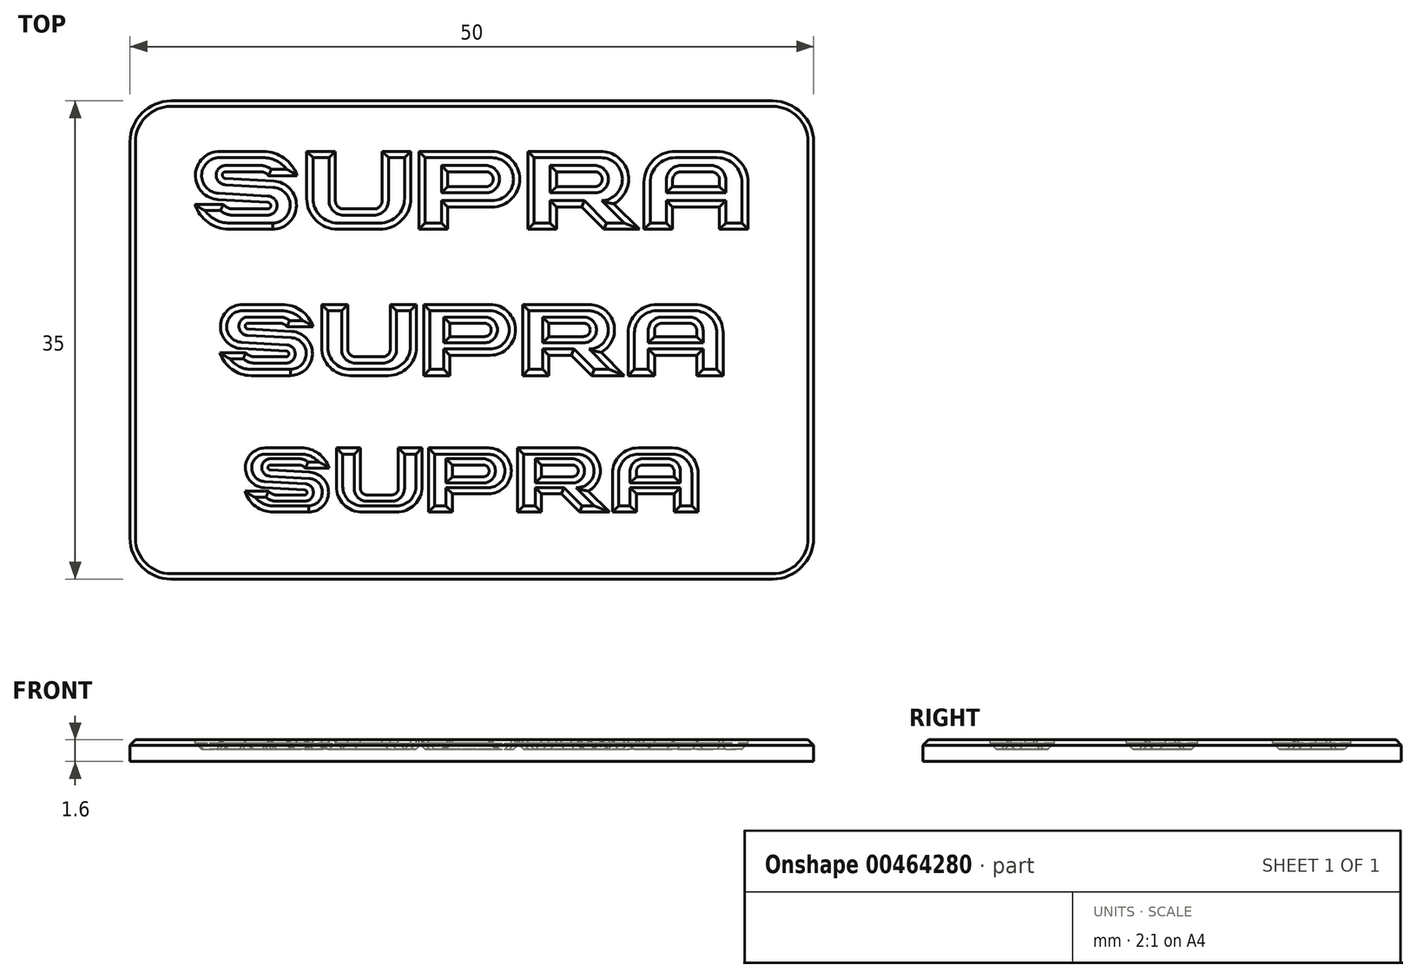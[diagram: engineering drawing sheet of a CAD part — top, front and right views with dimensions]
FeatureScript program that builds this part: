
annotation { "Feature Type Name" : "Feature", "Feature Type Description" : "" }
export const myFeature = defineFeature(function(context is Context, id is Id, definition is map)
    precondition{}
    {
        {
            var Q0;
            Q0=qCreatedBy(makeId("Top.planeOp"),FACE);
            var sketch = newSketch(context, id + "F0", { "sketchPlane" : qUnion([Q0])});
            skLineSegment(sketch, "E0.0", {"start": v(-11.75, 3.57) * mm, "end": v(-13.47, 3.57) * mm});
            skLineSegment(sketch, "E0.1", {"start": v(-14.02, 3.83) * mm, "end": v(-16.36, 3.83) * mm});
            skLineSegment(sketch, "E0.2", {"start": v(-15.88, 1.17) * mm, "end": v(-13.59, 1.17) * mm});
            skLineSegment(sketch, "E0.4", {"start": v(-16.57, 1.48) * mm, "end": v(-18.29, 1.48) * mm});
            skLineSegment(sketch, "E1", {"start": v(-16.86, 1.98) * mm, "end": v(-13.57, 1.8) * mm});
            skLineSegment(sketch, "E2", {"start": v(-16.38, 3.2) * mm, "end": v(-13.18, 3.03) * mm});
            skLineSegment(sketch, "E3.13", {"start": v(-6.12, 0) * mm, "end": v(-8.91, 0) * mm});
            skLineSegment(sketch, "E3.14", {"start": v(-8.52, 1.17) * mm, "end": v(-6.5, 1.17) * mm});
            skLineSegment(sketch, "E3.15", {"start": v(-9.17, 5) * mm, "end": v(-9.17, 1.81) * mm});
            skLineSegment(sketch, "E3.16", {"start": v(-10.89, 1.98) * mm, "end": v(-10.89, 5) * mm});
            skLineSegment(sketch, "E3.17", {"start": v(-10.89, 5) * mm, "end": v(-9.17, 5) * mm});
            skLineSegment(sketch, "E3.18", {"start": v(-5.87, 5) * mm, "end": v(-4.14, 5) * mm});
            skLineSegment(sketch, "E3.19", {"start": v(-4.14, 5) * mm, "end": v(-4.14, 1.98) * mm});
            skLineSegment(sketch, "E3.20", {"start": v(-5.87, 1.81) * mm, "end": v(-5.87, 5) * mm});
            skLineSegment(sketch, "E4.0", {"start": v(-3.42, 5) * mm, "end": v(1.34, 5) * mm});
            skLineSegment(sketch, "E4.1", {"start": v(0.94, 3.83) * mm, "end": v(-1.7, 3.83) * mm});
            skLineSegment(sketch, "E4.2", {"start": v(-1.7, 3.83) * mm, "end": v(-1.7, 2.66) * mm});
            skLineSegment(sketch, "E4.3", {"start": v(-1.7, 2.66) * mm, "end": v(0.94, 2.66) * mm});
            skLineSegment(sketch, "E4.4", {"start": v(1.34, 1.48) * mm, "end": v(-1.7, 1.48) * mm});
            skLineSegment(sketch, "E4.5", {"start": v(-1.7, 1.48) * mm, "end": v(-1.7, 0) * mm});
            skLineSegment(sketch, "E4.6", {"start": v(-3.42, 0) * mm, "end": v(-3.42, 5) * mm});
            skLineSegment(sketch, "E4.7", {"start": v(-1.7, 0) * mm, "end": v(-3.42, 0) * mm});
            skLineSegment(sketch, "E5.0", {"start": v(7.34, 1.48) * mm, "end": v(5.55, 1.48) * mm});
            skLineSegment(sketch, "E5.1", {"start": v(5.55, 1.48) * mm, "end": v(5.55, 0) * mm});
            skLineSegment(sketch, "E5.2", {"start": v(5.55, 0) * mm, "end": v(3.82, 0) * mm});
            skLineSegment(sketch, "E5.3", {"start": v(5.55, 2.66) * mm, "end": v(8.18, 2.66) * mm});
            skLineSegment(sketch, "E5.4", {"start": v(5.55, 3.83) * mm, "end": v(5.55, 2.66) * mm});
            skLineSegment(sketch, "E5.5", {"start": v(8.18, 3.83) * mm, "end": v(5.55, 3.83) * mm});
            skLineSegment(sketch, "E5.6", {"start": v(3.82, 5) * mm, "end": v(8.58, 5) * mm});
            skLineSegment(sketch, "E5.7", {"start": v(3.82, 0) * mm, "end": v(3.82, 5) * mm});
            skLineSegment(sketch, "E5.8", {"start": v(8.82, 0) * mm, "end": v(7.34, 1.48) * mm});
            skLineSegment(sketch, "E5.9", {"start": v(9.3, 1.63) * mm, "end": v(10.93, 0) * mm});
            skLineSegment(sketch, "E5.10", {"start": v(10.93, 0) * mm, "end": v(8.82, 0) * mm});
            skLineSegment(sketch, "E6.0", {"start": v(13.52, 5) * mm, "end": v(16.31, 5) * mm});
            skLineSegment(sketch, "E6.1", {"start": v(15.92, 3.83) * mm, "end": v(13.9, 3.83) * mm});
            skLineSegment(sketch, "E6.2", {"start": v(13.27, 3.19) * mm, "end": v(13.27, 2.66) * mm});
            skLineSegment(sketch, "E6.3", {"start": v(13.27, 2.66) * mm, "end": v(16.57, 2.66) * mm});
            skLineSegment(sketch, "E6.4", {"start": v(16.57, 2.66) * mm, "end": v(16.57, 3.19) * mm});
            skLineSegment(sketch, "E6.5", {"start": v(16.57, 1.48) * mm, "end": v(13.27, 1.48) * mm});
            skLineSegment(sketch, "E6.6", {"start": v(11.54, 0) * mm, "end": v(11.54, 3.02) * mm});
            skLineSegment(sketch, "E6.7", {"start": v(13.27, 0) * mm, "end": v(11.54, 0) * mm});
            skLineSegment(sketch, "E6.8", {"start": v(13.27, 1.48) * mm, "end": v(13.27, 0) * mm});
            skLineSegment(sketch, "E6.9", {"start": v(16.57, 0) * mm, "end": v(16.57, 1.48) * mm});
            skLineSegment(sketch, "E6.10", {"start": v(18.29, 0) * mm, "end": v(16.57, 0) * mm});
            skLineSegment(sketch, "E6.11", {"start": v(18.29, 3.02) * mm, "end": v(18.29, 0) * mm});
            skLineSegment(sketch, "E7", {"start": v(-7.52, 1.17) * mm, "end": v(-7.52, 0) * mm, "construction": true});
            skLineSegment(sketch, "E8", {"start": v(14.92, 3.83) * mm, "end": v(14.92, 5) * mm, "construction": true});
            skLineSegment(sketch, "E9", {"start": v(3.82, 0) * mm, "end": v(8.82, 0) * mm, "construction": true});
            skLineSegment(sketch, "E10", {"start": v(-1.7, 3.83) * mm, "end": v(-1.7, 5) * mm, "construction": true});
            skLineSegment(sketch, "E11", {"start": v(-1.7, 1.48) * mm, "end": v(-1.7, 2.66) * mm, "construction": true});
            skLineSegment(sketch, "E12", {"start": v(5.55, 1.48) * mm, "end": v(5.55, 2.66) * mm, "construction": true});
            skLineSegment(sketch, "E13", {"start": v(5.55, 3.83) * mm, "end": v(5.55, 5) * mm, "construction": true});
            skArc(sketch, "E14", {"start": v(-16.38, 3.2) * mm, "mid": v(-16.67, 3.52) * mm, "end": v(-16.36, 3.83) * mm});
            skArc(sketch, "E15", {"start": v(-14.02, 3.83) * mm, "mid": v(-13.72, 3.76) * mm, "end": v(-13.47, 3.57) * mm});
            skArc(sketch, "E16", {"start": v(-15.88, 1.17) * mm, "mid": v(-16.26, 1.25) * mm, "end": v(-16.57, 1.48) * mm});
            skArc(sketch, "E17", {"start": v(-13.57, 1.8) * mm, "mid": v(-13.27, 1.48) * mm, "end": v(-13.59, 1.17) * mm});
            skArc(sketch, "E18", {"start": v(-13.86, 5) * mm, "mid": v(-12.59, 4.61) * mm, "end": v(-11.75, 3.57) * mm});
            skArc(sketch, "E19", {"start": v(-16.13, 0) * mm, "mid": v(-17.44, 0.4) * mm, "end": v(-18.29, 1.48) * mm});
            skArc(sketch, "E20", {"start": v(-8.52, 1.17) * mm, "mid": v(-8.98, 1.36) * mm, "end": v(-9.17, 1.81) * mm});
            skArc(sketch, "E21", {"start": v(-6.5, 1.17) * mm, "mid": v(-6.05, 1.36) * mm, "end": v(-5.87, 1.81) * mm});
            skArc(sketch, "E22", {"start": v(-8.91, 0) * mm, "mid": v(-10.3, 0.58) * mm, "end": v(-10.89, 1.98) * mm});
            skArc(sketch, "E23", {"start": v(-6.12, 0) * mm, "mid": v(-4.72, 0.58) * mm, "end": v(-4.14, 1.98) * mm});
            skArc(sketch, "E24", {"start": v(1.34, 5) * mm, "mid": v(3.1, 3.24) * mm, "end": v(1.34, 1.48) * mm});
            skArc(sketch, "E25", {"start": v(0.94, 3.83) * mm, "mid": v(1.52, 3.24) * mm, "end": v(0.94, 2.66) * mm});
            skArc(sketch, "E26", {"start": v(8.18, 3.83) * mm, "mid": v(8.76, 3.24) * mm, "end": v(8.18, 2.66) * mm});
            skArc(sketch, "E27", {"start": v(13.9, 3.83) * mm, "mid": v(13.45, 3.64) * mm, "end": v(13.27, 3.19) * mm});
            skArc(sketch, "E28", {"start": v(15.92, 3.83) * mm, "mid": v(16.38, 3.64) * mm, "end": v(16.57, 3.19) * mm});
            skArc(sketch, "E29", {"start": v(13.52, 5) * mm, "mid": v(12.12, 4.42) * mm, "end": v(11.54, 3.02) * mm});
            skArc(sketch, "E30", {"start": v(16.31, 5) * mm, "mid": v(17.7, 4.42) * mm, "end": v(18.29, 3.02) * mm});
            skLineSegment(sketch, "E31", {"start": v(-9.17, 1.81) * mm, "end": v(-5.87, 1.81) * mm, "construction": true});
            skArc(sketch, "E32", {"start": v(8.58, 5) * mm, "mid": v(10.3, 3.6) * mm, "end": v(9.3, 1.63) * mm});
            skArc(sketch, "E33", {"start": v(-16.86, 1.98) * mm, "mid": v(-18.29, 3.53) * mm, "end": v(-16.78, 5) * mm});
            skLineSegment(sketch, "E34", {"start": v(-13.86, 5) * mm, "end": v(-16.78, 5) * mm});
            skArc(sketch, "E35", {"start": v(-13.18, 3.03) * mm, "mid": v(-11.75, 1.48) * mm, "end": v(-13.25, 0) * mm});
            skLineSegment(sketch, "E36", {"start": v(-16.13, 0) * mm, "end": v(-13.25, 0) * mm});
            skLineSegment(sketch, "E37.bottom", {"start": v(-18.29, 5) * mm, "end": v(18.29, 5) * mm, "construction": true});
            skLineSegment(sketch, "E37.top", {"start": v(-18.29, 0) * mm, "end": v(18.29, 0) * mm, "construction": true});
            skLineSegment(sketch, "E37.left", {"start": v(-18.29, 5) * mm, "end": v(-18.29, 0) * mm, "construction": true});
            skLineSegment(sketch, "E37.right", {"start": v(18.29, 5) * mm, "end": v(18.29, 0) * mm, "construction": true});
            skLineSegment(sketch, "E38", {"start": v(1.52, 3.24) * mm, "end": v(3.1, 3.24) * mm, "construction": true});
            skLineSegment(sketch, "E39", {"start": v(8.76, 3.24) * mm, "end": v(10.34, 3.24) * mm, "construction": true});
            skLineSegment(sketch, "E40", {"start": v(3.1, 3.24) * mm, "end": v(3.82, 3.24) * mm, "construction": true});
            skLineSegment(sketch, "E41", {"start": v(-4.14, 3.24) * mm, "end": v(-3.42, 3.24) * mm, "construction": true});
            skPoint(sketch, "E42", {"position": v(-11.75, 1.48) * mm});
            skSolve(sketch);
        }
        {
            var Q0;
            Q0=qCreatedBy(makeId("Top.planeOp"),FACE);
            var sketch = newSketch(context, id + "F1", { "sketchPlane" : qUnion([Q0])});
            skLineSegment(sketch, "E43.0", {"start": v(-12.93, 14.64) * mm, "end": v(-14.82, 14.64) * mm});
            skLineSegment(sketch, "E43.1", {"start": v(-15.43, 14.92) * mm, "end": v(-18, 14.92) * mm});
            skLineSegment(sketch, "E43.2", {"start": v(-17.47, 12) * mm, "end": v(-14.95, 12) * mm});
            skLineSegment(sketch, "E43.4", {"start": v(-18.22, 12.34) * mm, "end": v(-20.12, 12.34) * mm});
            skLineSegment(sketch, "E44", {"start": v(-18.54, 12.88) * mm, "end": v(-14.93, 12.68) * mm});
            skLineSegment(sketch, "E45", {"start": v(-18.02, 14.23) * mm, "end": v(-14.5, 14.04) * mm});
            skLineSegment(sketch, "E46.13", {"start": v(-6.73, 10.7) * mm, "end": v(-9.8, 10.7) * mm});
            skLineSegment(sketch, "E46.14", {"start": v(-9.37, 12) * mm, "end": v(-7.16, 12) * mm});
            skLineSegment(sketch, "E46.15", {"start": v(-10.08, 16.2) * mm, "end": v(-10.08, 12.7) * mm});
            skLineSegment(sketch, "E46.16", {"start": v(-11.98, 12.88) * mm, "end": v(-11.98, 16.2) * mm});
            skLineSegment(sketch, "E46.17", {"start": v(-11.98, 16.2) * mm, "end": v(-10.08, 16.2) * mm});
            skLineSegment(sketch, "E46.18", {"start": v(-6.45, 16.2) * mm, "end": v(-4.56, 16.2) * mm});
            skLineSegment(sketch, "E46.19", {"start": v(-4.56, 16.2) * mm, "end": v(-4.56, 12.88) * mm});
            skLineSegment(sketch, "E46.20", {"start": v(-6.45, 12.7) * mm, "end": v(-6.45, 16.2) * mm});
            skLineSegment(sketch, "E47.0", {"start": v(-3.76, 16.2) * mm, "end": v(1.48, 16.2) * mm});
            skLineSegment(sketch, "E47.1", {"start": v(1.03, 14.92) * mm, "end": v(-1.87, 14.92) * mm});
            skLineSegment(sketch, "E47.2", {"start": v(-1.87, 14.92) * mm, "end": v(-1.87, 13.63) * mm});
            skLineSegment(sketch, "E47.3", {"start": v(-1.87, 13.63) * mm, "end": v(1.03, 13.63) * mm});
            skLineSegment(sketch, "E47.4", {"start": v(1.48, 12.34) * mm, "end": v(-1.87, 12.34) * mm});
            skLineSegment(sketch, "E47.5", {"start": v(-1.87, 12.34) * mm, "end": v(-1.87, 10.7) * mm});
            skLineSegment(sketch, "E47.6", {"start": v(-3.76, 10.7) * mm, "end": v(-3.76, 16.2) * mm});
            skLineSegment(sketch, "E47.7", {"start": v(-1.87, 10.7) * mm, "end": v(-3.76, 10.7) * mm});
            skLineSegment(sketch, "E48.0", {"start": v(8.07, 12.34) * mm, "end": v(6.1, 12.34) * mm});
            skLineSegment(sketch, "E48.1", {"start": v(6.1, 12.34) * mm, "end": v(6.1, 10.7) * mm});
            skLineSegment(sketch, "E48.2", {"start": v(6.1, 10.7) * mm, "end": v(4.2, 10.7) * mm});
            skLineSegment(sketch, "E48.3", {"start": v(6.1, 13.63) * mm, "end": v(9, 13.63) * mm});
            skLineSegment(sketch, "E48.4", {"start": v(6.1, 14.92) * mm, "end": v(6.1, 13.63) * mm});
            skLineSegment(sketch, "E48.5", {"start": v(9, 14.92) * mm, "end": v(6.1, 14.92) * mm});
            skLineSegment(sketch, "E48.6", {"start": v(4.2, 16.2) * mm, "end": v(9.44, 16.2) * mm});
            skLineSegment(sketch, "E48.7", {"start": v(4.2, 10.7) * mm, "end": v(4.2, 16.2) * mm});
            skLineSegment(sketch, "E48.8", {"start": v(9.7, 10.7) * mm, "end": v(8.07, 12.34) * mm});
            skLineSegment(sketch, "E48.9", {"start": v(10.22, 12.5) * mm, "end": v(12.02, 10.7) * mm});
            skLineSegment(sketch, "E48.10", {"start": v(12.02, 10.7) * mm, "end": v(9.7, 10.7) * mm});
            skLineSegment(sketch, "E49.0", {"start": v(14.87, 16.2) * mm, "end": v(17.94, 16.2) * mm});
            skLineSegment(sketch, "E49.1", {"start": v(17.51, 14.92) * mm, "end": v(15.3, 14.92) * mm});
            skLineSegment(sketch, "E49.2", {"start": v(14.6, 14.2) * mm, "end": v(14.6, 13.63) * mm});
            skLineSegment(sketch, "E49.3", {"start": v(14.6, 13.63) * mm, "end": v(18.22, 13.63) * mm});
            skLineSegment(sketch, "E49.4", {"start": v(18.22, 13.63) * mm, "end": v(18.22, 14.2) * mm});
            skLineSegment(sketch, "E49.5", {"start": v(18.22, 12.34) * mm, "end": v(14.6, 12.34) * mm});
            skLineSegment(sketch, "E49.6", {"start": v(12.7, 10.7) * mm, "end": v(12.7, 14.03) * mm});
            skLineSegment(sketch, "E49.7", {"start": v(14.6, 10.7) * mm, "end": v(12.7, 10.7) * mm});
            skLineSegment(sketch, "E49.8", {"start": v(14.6, 12.34) * mm, "end": v(14.6, 10.7) * mm});
            skLineSegment(sketch, "E49.9", {"start": v(18.22, 10.7) * mm, "end": v(18.22, 12.34) * mm});
            skLineSegment(sketch, "E49.10", {"start": v(20.12, 10.7) * mm, "end": v(18.22, 10.7) * mm});
            skLineSegment(sketch, "E49.11", {"start": v(20.12, 14.03) * mm, "end": v(20.12, 10.7) * mm});
            skLineSegment(sketch, "E50", {"start": v(-8.27, 12) * mm, "end": v(-8.27, 10.7) * mm, "construction": true});
            skLineSegment(sketch, "E51", {"start": v(16.4, 14.92) * mm, "end": v(16.4, 16.2) * mm, "construction": true});
            skLineSegment(sketch, "E52", {"start": v(4.2, 10.7) * mm, "end": v(9.7, 10.7) * mm, "construction": true});
            skLineSegment(sketch, "E53", {"start": v(-1.87, 14.92) * mm, "end": v(-1.87, 16.2) * mm, "construction": true});
            skLineSegment(sketch, "E54", {"start": v(-1.87, 12.34) * mm, "end": v(-1.87, 13.63) * mm, "construction": true});
            skLineSegment(sketch, "E55", {"start": v(6.1, 12.34) * mm, "end": v(6.1, 13.63) * mm, "construction": true});
            skLineSegment(sketch, "E56", {"start": v(6.1, 14.92) * mm, "end": v(6.1, 16.2) * mm, "construction": true});
            skArc(sketch, "E57", {"start": v(-18.02, 14.23) * mm, "mid": v(-18.34, 14.58) * mm, "end": v(-18, 14.92) * mm});
            skArc(sketch, "E58", {"start": v(-15.43, 14.92) * mm, "mid": v(-15.1, 14.84) * mm, "end": v(-14.82, 14.64) * mm});
            skArc(sketch, "E59", {"start": v(-17.47, 12) * mm, "mid": v(-17.88, 12.09) * mm, "end": v(-18.22, 12.34) * mm});
            skArc(sketch, "E60", {"start": v(-14.93, 12.68) * mm, "mid": v(-14.6, 12.33) * mm, "end": v(-14.95, 12) * mm});
            skArc(sketch, "E61", {"start": v(-15.25, 16.2) * mm, "mid": v(-13.85, 15.78) * mm, "end": v(-12.93, 14.64) * mm});
            skArc(sketch, "E62", {"start": v(-17.74, 10.7) * mm, "mid": v(-19.19, 11.15) * mm, "end": v(-20.12, 12.34) * mm});
            skArc(sketch, "E63", {"start": v(-9.37, 12) * mm, "mid": v(-9.87, 12.2) * mm, "end": v(-10.08, 12.7) * mm});
            skArc(sketch, "E64", {"start": v(-7.16, 12) * mm, "mid": v(-6.66, 12.2) * mm, "end": v(-6.45, 12.7) * mm});
            skArc(sketch, "E65", {"start": v(-9.8, 10.7) * mm, "mid": v(-11.34, 11.34) * mm, "end": v(-11.98, 12.88) * mm});
            skArc(sketch, "E66", {"start": v(-6.73, 10.7) * mm, "mid": v(-5.2, 11.34) * mm, "end": v(-4.56, 12.88) * mm});
            skArc(sketch, "E67", {"start": v(1.48, 16.2) * mm, "mid": v(3.4, 14.27) * mm, "end": v(1.48, 12.34) * mm});
            skArc(sketch, "E68", {"start": v(1.03, 14.92) * mm, "mid": v(1.67, 14.27) * mm, "end": v(1.03, 13.63) * mm});
            skArc(sketch, "E69", {"start": v(9, 14.92) * mm, "mid": v(9.64, 14.27) * mm, "end": v(9, 13.63) * mm});
            skArc(sketch, "E70", {"start": v(15.3, 14.92) * mm, "mid": v(14.8, 14.7) * mm, "end": v(14.6, 14.2) * mm});
            skArc(sketch, "E71", {"start": v(17.51, 14.92) * mm, "mid": v(18.01, 14.7) * mm, "end": v(18.22, 14.2) * mm});
            skArc(sketch, "E72", {"start": v(14.87, 16.2) * mm, "mid": v(13.33, 15.57) * mm, "end": v(12.7, 14.03) * mm});
            skArc(sketch, "E73", {"start": v(17.94, 16.2) * mm, "mid": v(19.48, 15.57) * mm, "end": v(20.12, 14.03) * mm});
            skLineSegment(sketch, "E74", {"start": v(-10.08, 12.7) * mm, "end": v(-6.45, 12.7) * mm, "construction": true});
            skArc(sketch, "E75", {"start": v(9.44, 16.2) * mm, "mid": v(11.33, 14.67) * mm, "end": v(10.22, 12.5) * mm});
            skArc(sketch, "E76", {"start": v(-18.54, 12.88) * mm, "mid": v(-20.12, 14.59) * mm, "end": v(-18.45, 16.2) * mm});
            skLineSegment(sketch, "E77", {"start": v(-15.25, 16.2) * mm, "end": v(-18.45, 16.2) * mm});
            skArc(sketch, "E78", {"start": v(-14.5, 14.04) * mm, "mid": v(-12.93, 12.34) * mm, "end": v(-14.57, 10.7) * mm});
            skLineSegment(sketch, "E79", {"start": v(-17.74, 10.7) * mm, "end": v(-14.57, 10.7) * mm});
            skLineSegment(sketch, "E80.bottom", {"start": v(-20.12, 16.2) * mm, "end": v(20.12, 16.2) * mm, "construction": true});
            skLineSegment(sketch, "E80.top", {"start": v(-20.12, 10.7) * mm, "end": v(20.12, 10.7) * mm, "construction": true});
            skLineSegment(sketch, "E80.left", {"start": v(-20.12, 16.2) * mm, "end": v(-20.12, 10.7) * mm, "construction": true});
            skLineSegment(sketch, "E80.right", {"start": v(20.12, 16.2) * mm, "end": v(20.12, 10.7) * mm, "construction": true});
            skLineSegment(sketch, "E81", {"start": v(1.67, 14.27) * mm, "end": v(3.4, 14.27) * mm, "construction": true});
            skLineSegment(sketch, "E82", {"start": v(9.64, 14.27) * mm, "end": v(11.38, 14.27) * mm, "construction": true});
            skLineSegment(sketch, "E83", {"start": v(3.4, 14.27) * mm, "end": v(4.2, 14.27) * mm, "construction": true});
            skLineSegment(sketch, "E84", {"start": v(-4.56, 14.27) * mm, "end": v(-3.76, 14.27) * mm, "construction": true});
            skPoint(sketch, "E85", {"position": v(-12.93, 12.34) * mm});
            skSolve(sketch);
        }
        {
            var Q0;
            Q0=qCreatedBy(makeId("Top.planeOp"),FACE);
            var sketch = newSketch(context, id + "F2", { "sketchPlane" : qUnion([Q0])});
            skLineSegment(sketch, "E86.0", {"start": v(-10.58, -6.78) * mm, "end": v(-12.13, -6.78) * mm});
            skLineSegment(sketch, "E86.1", {"start": v(-12.62, -6.55) * mm, "end": v(-14.73, -6.55) * mm});
            skLineSegment(sketch, "E86.2", {"start": v(-14.3, -8.94) * mm, "end": v(-12.23, -8.94) * mm});
            skLineSegment(sketch, "E86.4", {"start": v(-14.9, -8.66) * mm, "end": v(-16.46, -8.66) * mm});
            skLineSegment(sketch, "E87", {"start": v(-15.17, -8.21) * mm, "end": v(-12.21, -8.38) * mm});
            skLineSegment(sketch, "E88", {"start": v(-14.74, -7.1) * mm, "end": v(-11.86, -7.27) * mm});
            skLineSegment(sketch, "E89.13", {"start": v(-5.5, -10) * mm, "end": v(-8.02, -10) * mm});
            skLineSegment(sketch, "E89.14", {"start": v(-7.67, -8.94) * mm, "end": v(-5.86, -8.94) * mm});
            skLineSegment(sketch, "E89.15", {"start": v(-8.25, -5.5) * mm, "end": v(-8.25, -8.36) * mm});
            skLineSegment(sketch, "E89.16", {"start": v(-9.8, -8.21) * mm, "end": v(-9.8, -5.5) * mm});
            skLineSegment(sketch, "E89.17", {"start": v(-9.8, -5.5) * mm, "end": v(-8.25, -5.5) * mm});
            skLineSegment(sketch, "E89.18", {"start": v(-5.28, -5.5) * mm, "end": v(-3.73, -5.5) * mm});
            skLineSegment(sketch, "E89.19", {"start": v(-3.73, -5.5) * mm, "end": v(-3.73, -8.21) * mm});
            skLineSegment(sketch, "E89.20", {"start": v(-5.28, -8.36) * mm, "end": v(-5.28, -5.5) * mm});
            skLineSegment(sketch, "E90.0", {"start": v(-3.08, -5.5) * mm, "end": v(1.2, -5.5) * mm});
            skLineSegment(sketch, "E90.1", {"start": v(0.84, -6.55) * mm, "end": v(-1.53, -6.55) * mm});
            skLineSegment(sketch, "E90.2", {"start": v(-1.53, -6.55) * mm, "end": v(-1.53, -7.6) * mm});
            skLineSegment(sketch, "E90.3", {"start": v(-1.53, -7.6) * mm, "end": v(0.84, -7.6) * mm});
            skLineSegment(sketch, "E90.4", {"start": v(1.2, -8.66) * mm, "end": v(-1.53, -8.66) * mm});
            skLineSegment(sketch, "E90.5", {"start": v(-1.53, -8.66) * mm, "end": v(-1.53, -10) * mm});
            skLineSegment(sketch, "E90.6", {"start": v(-3.08, -10) * mm, "end": v(-3.08, -5.5) * mm});
            skLineSegment(sketch, "E90.7", {"start": v(-1.53, -10) * mm, "end": v(-3.08, -10) * mm});
            skLineSegment(sketch, "E91.0", {"start": v(6.6, -8.66) * mm, "end": v(5, -8.66) * mm});
            skLineSegment(sketch, "E91.1", {"start": v(5, -8.66) * mm, "end": v(5, -10) * mm});
            skLineSegment(sketch, "E91.2", {"start": v(5, -10) * mm, "end": v(3.44, -10) * mm});
            skLineSegment(sketch, "E91.3", {"start": v(5, -7.6) * mm, "end": v(7.36, -7.6) * mm});
            skLineSegment(sketch, "E91.4", {"start": v(5, -6.55) * mm, "end": v(5, -7.6) * mm});
            skLineSegment(sketch, "E91.5", {"start": v(7.36, -6.55) * mm, "end": v(5, -6.55) * mm});
            skLineSegment(sketch, "E91.6", {"start": v(3.44, -5.5) * mm, "end": v(7.73, -5.5) * mm});
            skLineSegment(sketch, "E91.7", {"start": v(3.44, -10) * mm, "end": v(3.44, -5.5) * mm});
            skLineSegment(sketch, "E91.8", {"start": v(7.94, -10) * mm, "end": v(6.6, -8.66) * mm});
            skLineSegment(sketch, "E91.9", {"start": v(8.36, -8.52) * mm, "end": v(9.83, -10) * mm});
            skLineSegment(sketch, "E91.10", {"start": v(9.83, -10) * mm, "end": v(7.94, -10) * mm});
            skLineSegment(sketch, "E92.0", {"start": v(12.17, -5.5) * mm, "end": v(14.68, -5.5) * mm});
            skLineSegment(sketch, "E92.1", {"start": v(14.33, -6.55) * mm, "end": v(12.52, -6.55) * mm});
            skLineSegment(sketch, "E92.2", {"start": v(11.94, -7.13) * mm, "end": v(11.94, -7.6) * mm});
            skLineSegment(sketch, "E92.3", {"start": v(11.94, -7.6) * mm, "end": v(14.9, -7.6) * mm});
            skLineSegment(sketch, "E92.4", {"start": v(14.9, -7.6) * mm, "end": v(14.9, -7.13) * mm});
            skLineSegment(sketch, "E92.5", {"start": v(14.9, -8.66) * mm, "end": v(11.94, -8.66) * mm});
            skLineSegment(sketch, "E92.6", {"start": v(10.39, -10) * mm, "end": v(10.39, -7.27) * mm});
            skLineSegment(sketch, "E92.7", {"start": v(11.94, -10) * mm, "end": v(10.39, -10) * mm});
            skLineSegment(sketch, "E92.8", {"start": v(11.94, -8.66) * mm, "end": v(11.94, -10) * mm});
            skLineSegment(sketch, "E92.9", {"start": v(14.9, -10) * mm, "end": v(14.9, -8.66) * mm});
            skLineSegment(sketch, "E92.10", {"start": v(16.46, -10) * mm, "end": v(14.9, -10) * mm});
            skLineSegment(sketch, "E92.11", {"start": v(16.46, -7.27) * mm, "end": v(16.46, -10) * mm});
            skLineSegment(sketch, "E93", {"start": v(-6.76, -8.94) * mm, "end": v(-6.76, -10) * mm, "construction": true});
            skLineSegment(sketch, "E94", {"start": v(13.42, -6.55) * mm, "end": v(13.42, -5.5) * mm, "construction": true});
            skLineSegment(sketch, "E95", {"start": v(3.44, -10) * mm, "end": v(7.94, -10) * mm, "construction": true});
            skLineSegment(sketch, "E96", {"start": v(-1.53, -6.55) * mm, "end": v(-1.53, -5.5) * mm, "construction": true});
            skLineSegment(sketch, "E97", {"start": v(-1.53, -8.66) * mm, "end": v(-1.53, -7.6) * mm, "construction": true});
            skLineSegment(sketch, "E98", {"start": v(5, -8.66) * mm, "end": v(5, -7.6) * mm, "construction": true});
            skLineSegment(sketch, "E99", {"start": v(5, -6.55) * mm, "end": v(5, -5.5) * mm, "construction": true});
            skArc(sketch, "E100", {"start": v(-14.74, -7.1) * mm, "mid": v(-15, -6.82) * mm, "end": v(-14.73, -6.55) * mm});
            skArc(sketch, "E101", {"start": v(-12.62, -6.55) * mm, "mid": v(-12.35, -6.6) * mm, "end": v(-12.13, -6.78) * mm});
            skArc(sketch, "E102", {"start": v(-14.3, -8.94) * mm, "mid": v(-14.63, -8.86) * mm, "end": v(-14.9, -8.66) * mm});
            skArc(sketch, "E103", {"start": v(-12.21, -8.38) * mm, "mid": v(-11.95, -8.67) * mm, "end": v(-12.23, -8.94) * mm});
            skArc(sketch, "E104", {"start": v(-12.48, -5.5) * mm, "mid": v(-11.33, -5.84) * mm, "end": v(-10.58, -6.78) * mm});
            skArc(sketch, "E105", {"start": v(-14.52, -10) * mm, "mid": v(-15.7, -9.63) * mm, "end": v(-16.46, -8.66) * mm});
            skArc(sketch, "E106", {"start": v(-7.67, -8.94) * mm, "mid": v(-8.08, -8.77) * mm, "end": v(-8.25, -8.36) * mm});
            skArc(sketch, "E107", {"start": v(-5.86, -8.94) * mm, "mid": v(-5.45, -8.77) * mm, "end": v(-5.28, -8.36) * mm});
            skArc(sketch, "E108", {"start": v(-8.02, -10) * mm, "mid": v(-9.28, -9.47) * mm, "end": v(-9.8, -8.21) * mm});
            skArc(sketch, "E109", {"start": v(-5.5, -10) * mm, "mid": v(-4.25, -9.47) * mm, "end": v(-3.73, -8.21) * mm});
            skArc(sketch, "E110", {"start": v(1.2, -5.5) * mm, "mid": v(2.79, -7.08) * mm, "end": v(1.2, -8.66) * mm});
            skArc(sketch, "E111", {"start": v(0.84, -6.55) * mm, "mid": v(1.37, -7.08) * mm, "end": v(0.84, -7.6) * mm});
            skArc(sketch, "E112", {"start": v(7.36, -6.55) * mm, "mid": v(7.89, -7.08) * mm, "end": v(7.36, -7.6) * mm});
            skArc(sketch, "E113", {"start": v(12.52, -6.55) * mm, "mid": v(12.1, -6.72) * mm, "end": v(11.94, -7.13) * mm});
            skArc(sketch, "E114", {"start": v(14.33, -6.55) * mm, "mid": v(14.74, -6.72) * mm, "end": v(14.9, -7.13) * mm});
            skArc(sketch, "E115", {"start": v(12.17, -5.5) * mm, "mid": v(10.9, -6.01) * mm, "end": v(10.39, -7.27) * mm});
            skArc(sketch, "E116", {"start": v(14.68, -5.5) * mm, "mid": v(15.94, -6.01) * mm, "end": v(16.46, -7.27) * mm});
            skLineSegment(sketch, "E117", {"start": v(-8.25, -8.36) * mm, "end": v(-5.28, -8.36) * mm, "construction": true});
            skArc(sketch, "E118", {"start": v(7.73, -5.5) * mm, "mid": v(9.27, -6.75) * mm, "end": v(8.36, -8.52) * mm});
            skArc(sketch, "E119", {"start": v(-15.17, -8.21) * mm, "mid": v(-16.46, -6.82) * mm, "end": v(-15.1, -5.5) * mm});
            skLineSegment(sketch, "E120", {"start": v(-12.48, -5.5) * mm, "end": v(-15.1, -5.5) * mm});
            skArc(sketch, "E121", {"start": v(-11.86, -7.27) * mm, "mid": v(-10.58, -8.66) * mm, "end": v(-11.92, -10) * mm});
            skLineSegment(sketch, "E122", {"start": v(-14.52, -10) * mm, "end": v(-11.92, -10) * mm});
            skLineSegment(sketch, "E123.bottom", {"start": v(-16.46, -5.5) * mm, "end": v(16.46, -5.5) * mm, "construction": true});
            skLineSegment(sketch, "E123.top", {"start": v(-16.46, -10) * mm, "end": v(16.46, -10) * mm, "construction": true});
            skLineSegment(sketch, "E123.left", {"start": v(-16.46, -5.5) * mm, "end": v(-16.46, -10) * mm, "construction": true});
            skLineSegment(sketch, "E123.right", {"start": v(16.46, -5.5) * mm, "end": v(16.46, -10) * mm, "construction": true});
            skLineSegment(sketch, "E124", {"start": v(1.37, -7.08) * mm, "end": v(2.79, -7.08) * mm, "construction": true});
            skLineSegment(sketch, "E125", {"start": v(7.89, -7.08) * mm, "end": v(9.3, -7.08) * mm, "construction": true});
            skLineSegment(sketch, "E126", {"start": v(2.79, -7.08) * mm, "end": v(3.44, -7.08) * mm, "construction": true});
            skLineSegment(sketch, "E127", {"start": v(-3.73, -7.08) * mm, "end": v(-3.08, -7.08) * mm, "construction": true});
            skPoint(sketch, "E128", {"position": v(-10.58, -8.66) * mm});
            skSolve(sketch);
        }
        {
            var Q0;
            Q0 = qSketchRegion(id + "F0", true);
            var Q1;
            Q1 = qSketchRegion(id + "F1", true);
            var Q2;
            Q2 = qSketchRegion(id + "F2", true);
            extrude(context, id + "F3", {"entities" : qUnion([Q0, Q1, Q2]), "oppositeDirection" : true, "depth" : 0.6 * mm, "offsetDistance" : 25 * mm});
        }
        {
            var Q0;
            Q0=qCreatedBy(makeId("Top.planeOp"),FACE);
            var sketch = newSketch(context, id + "F4", { "sketchPlane" : qUnion([Q0])});
            skLineSegment(sketch, "E129.bottom", {"start": v(22, -15) * mm, "end": v(-22, -15) * mm});
            skLineSegment(sketch, "E129.top", {"start": v(22, 20) * mm, "end": v(-22, 20) * mm});
            skLineSegment(sketch, "E129.left", {"start": v(25, -12) * mm, "end": v(25, 17) * mm});
            skLineSegment(sketch, "E129.right", {"start": v(-25, -12) * mm, "end": v(-25, 17) * mm});
            skPoint(sketch, "E129.middle", {"position": v(0, 2.5) * mm});
            skPoint(sketch, "E130.visualSharp", {"position": v(-25, 20) * mm});
            skArc(sketch, "E130.filletArc", {"start": v(-22, 20) * mm, "mid": v(-24.12, 19.12) * mm, "end": v(-25, 17) * mm});
            skPoint(sketch, "E131.visualSharp", {"position": v(-25, -15) * mm});
            skArc(sketch, "E131.filletArc", {"start": v(-25, -12) * mm, "mid": v(-24.12, -14.12) * mm, "end": v(-22, -15) * mm});
            skPoint(sketch, "E132.visualSharp", {"position": v(25, -15) * mm});
            skArc(sketch, "E132.filletArc", {"start": v(22, -15) * mm, "mid": v(24.12, -14.12) * mm, "end": v(25, -12) * mm});
            skPoint(sketch, "E133.visualSharp", {"position": v(25, 20) * mm});
            skArc(sketch, "E133.filletArc", {"start": v(25, 17) * mm, "mid": v(24.12, 19.12) * mm, "end": v(22, 20) * mm});
            skSolve(sketch);
        }
        {
            var Q0;
            Q0 = qSketchRegion(id + "F4", true);
            extrude(context, id + "F5", {"entities" : qUnion([Q0]), "oppositeDirection" : true, "depth" : 1.6 * mm, "offsetDistance" : 25 * mm});
        }
        {
            var Q0;
            Q0=makeQuery(id+"F3.opExtrude","CAP_FACE",FACE,{"disambiguationData":[OSD([sQuery(id+"F0.wireOp",EDGE,"E0.0"),sQuery(id+"F0.wireOp",EDGE,"E0.1"),sQuery(id+"F0.wireOp",EDGE,"E0.2"),sQuery(id+"F0.wireOp",EDGE,"E0.3"),sQuery(id+"F0.wireOp",EDGE,"E0.4"),sQuery(id+"F0.wireOp",EDGE,"0999620a-5725-4c23-bbf2-5b95b2830843"),sQuery(id+"F0.wireOp",EDGE,"386d07d4-47ab-48fc-b2f3-6c93ff8b900a"),sQuery(id+"F0.wireOp",EDGE,"7d214aef-e285-4256-be08-b174b5a9389a"),sQuery(id+"F0.wireOp",EDGE,"1d019c9d-348e-44f8-a51e-25f3e83873e8"),sQuery(id+"F0.wireOp",EDGE,"8814e4d5-f851-4526-9bd3-24134bf95cf7"),sQuery(id+"F0.wireOp",EDGE,"854dbfa7-0297-4156-a36c-3462ac4aca29"),sQuery(id+"F0.wireOp",EDGE,"68418355-34de-4963-a5e1-fe12fbad6afa"),sQuery(id+"F0.wireOp",EDGE,"0ad70b45-b280-4e47-a12a-156df6aa18f4"),sQuery(id+"F0.wireOp",EDGE,"909f7516-75d9-4176-a7ec-8d11efcea972.0"),sQuery(id+"F0.wireOp",EDGE,"E1"),sQuery(id+"F0.wireOp",EDGE,"E2")])],"isStart":false});
            var Q1;
            Q1=makeQuery(id+"F3.opExtrude","CAP_FACE",FACE,{"disambiguationData":[OSD([sQuery(id+"F0.wireOp",EDGE,"E3.13"),sQuery(id+"F0.wireOp",EDGE,"E3.14"),sQuery(id+"F0.wireOp",EDGE,"E3.15"),sQuery(id+"F0.wireOp",EDGE,"E3.16"),sQuery(id+"F0.wireOp",EDGE,"E3.17"),sQuery(id+"F0.wireOp",EDGE,"E3.18"),sQuery(id+"F0.wireOp",EDGE,"E3.19"),sQuery(id+"F0.wireOp",EDGE,"E3.20"),sQuery(id+"F0.wireOp",EDGE,"18193e6a-b45a-4486-8c24-13befce3e4da"),sQuery(id+"F0.wireOp",EDGE,"87248437-bed7-459e-b474-820dd873d0e6"),sQuery(id+"F0.wireOp",EDGE,"dfc161e1-bacf-4af8-9d18-555532bfa341"),sQuery(id+"F0.wireOp",EDGE,"dfd43905-2174-4bfa-a2d9-08ca3ab83ac5")])],"isStart":false});
            var Q2;
            Q2=makeQuery(id+"F3.opExtrude","CAP_FACE",FACE,{"disambiguationData":[OSD([sQuery(id+"F0.wireOp",EDGE,"E4.0"),sQuery(id+"F0.wireOp",EDGE,"E4.1"),sQuery(id+"F0.wireOp",EDGE,"E4.2"),sQuery(id+"F0.wireOp",EDGE,"E4.3"),sQuery(id+"F0.wireOp",EDGE,"E4.4"),sQuery(id+"F0.wireOp",EDGE,"E4.5"),sQuery(id+"F0.wireOp",EDGE,"E4.6"),sQuery(id+"F0.wireOp",EDGE,"E4.7"),sQuery(id+"F0.wireOp",EDGE,"109b3e3a-7d6f-4e72-87ea-cb87c5d67c68"),sQuery(id+"F0.wireOp",EDGE,"418c2995-c520-4838-b757-5a34ee8e35cc")])],"isStart":false});
            var Q3;
            Q3=makeQuery(id+"F3.opExtrude","CAP_FACE",FACE,{"disambiguationData":[OSD([sQuery(id+"F0.wireOp",EDGE,"E5.0"),sQuery(id+"F0.wireOp",EDGE,"E5.1"),sQuery(id+"F0.wireOp",EDGE,"E5.2"),sQuery(id+"F0.wireOp",EDGE,"E5.3"),sQuery(id+"F0.wireOp",EDGE,"E5.4"),sQuery(id+"F0.wireOp",EDGE,"E5.5"),sQuery(id+"F0.wireOp",EDGE,"E5.6"),sQuery(id+"F0.wireOp",EDGE,"E5.7"),sQuery(id+"F0.wireOp",EDGE,"E5.8"),sQuery(id+"F0.wireOp",EDGE,"E5.9"),sQuery(id+"F0.wireOp",EDGE,"E5.10"),sQuery(id+"F0.wireOp",EDGE,"826e8434-5312-4b00-bb0e-243ee4ab690c"),sQuery(id+"F0.wireOp",EDGE,"61057553-3613-4276-97cf-7665bd9cf830")])],"isStart":false});
            var Q4;
            Q4=makeQuery(id+"F3.opExtrude","CAP_FACE",FACE,{"disambiguationData":[OSD([sQuery(id+"F0.wireOp",EDGE,"E6.0"),sQuery(id+"F0.wireOp",EDGE,"E6.1"),sQuery(id+"F0.wireOp",EDGE,"E6.2"),sQuery(id+"F0.wireOp",EDGE,"E6.3"),sQuery(id+"F0.wireOp",EDGE,"E6.4"),sQuery(id+"F0.wireOp",EDGE,"E6.5"),sQuery(id+"F0.wireOp",EDGE,"E6.6"),sQuery(id+"F0.wireOp",EDGE,"E6.7"),sQuery(id+"F0.wireOp",EDGE,"E6.8"),sQuery(id+"F0.wireOp",EDGE,"E6.9"),sQuery(id+"F0.wireOp",EDGE,"E6.10"),sQuery(id+"F0.wireOp",EDGE,"E6.11"),sQuery(id+"F0.wireOp",EDGE,"99e759a4-61d7-4b6e-b7ee-9723b9a24aa8"),sQuery(id+"F0.wireOp",EDGE,"a95c86a1-a8cb-4604-8402-e9795dd98b0d"),sQuery(id+"F0.wireOp",EDGE,"d81874d2-dd95-4ed2-8042-69ce277cbfb6"),sQuery(id+"F0.wireOp",EDGE,"669a06dd-cf1c-428e-8a50-f27afc4aee4d")])],"isStart":false});
            var Q5;
            Q5=makeQuery(id+"F3.opExtrude","CAP_FACE",FACE,{"disambiguationData":[OSD([sQuery(id+"F2.wireOp",EDGE,"E92.0"),sQuery(id+"F2.wireOp",EDGE,"E92.1"),sQuery(id+"F2.wireOp",EDGE,"E92.2"),sQuery(id+"F2.wireOp",EDGE,"E92.3"),sQuery(id+"F2.wireOp",EDGE,"E92.4"),sQuery(id+"F2.wireOp",EDGE,"E92.5"),sQuery(id+"F2.wireOp",EDGE,"E92.6"),sQuery(id+"F2.wireOp",EDGE,"E92.7"),sQuery(id+"F2.wireOp",EDGE,"E92.8"),sQuery(id+"F2.wireOp",EDGE,"E92.9"),sQuery(id+"F2.wireOp",EDGE,"E92.10"),sQuery(id+"F2.wireOp",EDGE,"E92.11"),sQuery(id+"F2.wireOp",EDGE,"E113"),sQuery(id+"F2.wireOp",EDGE,"E114"),sQuery(id+"F2.wireOp",EDGE,"E115"),sQuery(id+"F2.wireOp",EDGE,"E116")])],"isStart":false});
            var Q6;
            Q6=makeQuery(id+"F3.opExtrude","CAP_FACE",FACE,{"disambiguationData":[OSD([sQuery(id+"F2.wireOp",EDGE,"E91.0"),sQuery(id+"F2.wireOp",EDGE,"E91.1"),sQuery(id+"F2.wireOp",EDGE,"E91.2"),sQuery(id+"F2.wireOp",EDGE,"E91.3"),sQuery(id+"F2.wireOp",EDGE,"E91.4"),sQuery(id+"F2.wireOp",EDGE,"E91.5"),sQuery(id+"F2.wireOp",EDGE,"E91.6"),sQuery(id+"F2.wireOp",EDGE,"E91.7"),sQuery(id+"F2.wireOp",EDGE,"E91.8"),sQuery(id+"F2.wireOp",EDGE,"E91.9"),sQuery(id+"F2.wireOp",EDGE,"E91.10"),sQuery(id+"F2.wireOp",EDGE,"E112"),sQuery(id+"F2.wireOp",EDGE,"E118")])],"isStart":false});
            var Q7;
            Q7=makeQuery(id+"F3.opExtrude","CAP_FACE",FACE,{"disambiguationData":[OSD([sQuery(id+"F2.wireOp",EDGE,"E90.0"),sQuery(id+"F2.wireOp",EDGE,"E90.1"),sQuery(id+"F2.wireOp",EDGE,"E90.2"),sQuery(id+"F2.wireOp",EDGE,"E90.3"),sQuery(id+"F2.wireOp",EDGE,"E90.4"),sQuery(id+"F2.wireOp",EDGE,"E90.5"),sQuery(id+"F2.wireOp",EDGE,"E90.6"),sQuery(id+"F2.wireOp",EDGE,"E90.7"),sQuery(id+"F2.wireOp",EDGE,"E110"),sQuery(id+"F2.wireOp",EDGE,"E111")])],"isStart":false});
            var Q8;
            Q8=makeQuery(id+"F3.opExtrude","CAP_FACE",FACE,{"disambiguationData":[OSD([sQuery(id+"F2.wireOp",EDGE,"E89.13"),sQuery(id+"F2.wireOp",EDGE,"E89.14"),sQuery(id+"F2.wireOp",EDGE,"E89.15"),sQuery(id+"F2.wireOp",EDGE,"E89.16"),sQuery(id+"F2.wireOp",EDGE,"E89.17"),sQuery(id+"F2.wireOp",EDGE,"E89.18"),sQuery(id+"F2.wireOp",EDGE,"E89.19"),sQuery(id+"F2.wireOp",EDGE,"E89.20"),sQuery(id+"F2.wireOp",EDGE,"E106"),sQuery(id+"F2.wireOp",EDGE,"E107"),sQuery(id+"F2.wireOp",EDGE,"E108"),sQuery(id+"F2.wireOp",EDGE,"E109")])],"isStart":false});
            var Q9;
            Q9=makeQuery(id+"F3.opExtrude","CAP_FACE",FACE,{"disambiguationData":[OSD([sQuery(id+"F2.wireOp",EDGE,"E86.0"),sQuery(id+"F2.wireOp",EDGE,"E86.1"),sQuery(id+"F2.wireOp",EDGE,"E86.2"),sQuery(id+"F2.wireOp",EDGE,"E86.4"),sQuery(id+"F2.wireOp",EDGE,"E87"),sQuery(id+"F2.wireOp",EDGE,"E88"),sQuery(id+"F2.wireOp",EDGE,"E100"),sQuery(id+"F2.wireOp",EDGE,"E101"),sQuery(id+"F2.wireOp",EDGE,"E102"),sQuery(id+"F2.wireOp",EDGE,"E103"),sQuery(id+"F2.wireOp",EDGE,"E104"),sQuery(id+"F2.wireOp",EDGE,"E105"),sQuery(id+"F2.wireOp",EDGE,"E119"),sQuery(id+"F2.wireOp",EDGE,"E120"),sQuery(id+"F2.wireOp",EDGE,"E121"),sQuery(id+"F2.wireOp",EDGE,"E122")])],"isStart":false});
            var Q10;
            Q10=makeQuery(id+"F3.opExtrude","CAP_FACE",FACE,{"disambiguationData":[OSD([sQuery(id+"F1.wireOp",EDGE,"E49.0"),sQuery(id+"F1.wireOp",EDGE,"E49.1"),sQuery(id+"F1.wireOp",EDGE,"E49.2"),sQuery(id+"F1.wireOp",EDGE,"E49.3"),sQuery(id+"F1.wireOp",EDGE,"E49.4"),sQuery(id+"F1.wireOp",EDGE,"E49.5"),sQuery(id+"F1.wireOp",EDGE,"E49.6"),sQuery(id+"F1.wireOp",EDGE,"E49.7"),sQuery(id+"F1.wireOp",EDGE,"E49.8"),sQuery(id+"F1.wireOp",EDGE,"E49.9"),sQuery(id+"F1.wireOp",EDGE,"E49.10"),sQuery(id+"F1.wireOp",EDGE,"E49.11"),sQuery(id+"F1.wireOp",EDGE,"E70"),sQuery(id+"F1.wireOp",EDGE,"E71"),sQuery(id+"F1.wireOp",EDGE,"E72"),sQuery(id+"F1.wireOp",EDGE,"E73")])],"isStart":false});
            var Q11;
            Q11=makeQuery(id+"F3.opExtrude","CAP_FACE",FACE,{"disambiguationData":[OSD([sQuery(id+"F1.wireOp",EDGE,"E48.0"),sQuery(id+"F1.wireOp",EDGE,"E48.1"),sQuery(id+"F1.wireOp",EDGE,"E48.2"),sQuery(id+"F1.wireOp",EDGE,"E48.3"),sQuery(id+"F1.wireOp",EDGE,"E48.4"),sQuery(id+"F1.wireOp",EDGE,"E48.5"),sQuery(id+"F1.wireOp",EDGE,"E48.6"),sQuery(id+"F1.wireOp",EDGE,"E48.7"),sQuery(id+"F1.wireOp",EDGE,"E48.8"),sQuery(id+"F1.wireOp",EDGE,"E48.9"),sQuery(id+"F1.wireOp",EDGE,"E48.10"),sQuery(id+"F1.wireOp",EDGE,"E69"),sQuery(id+"F1.wireOp",EDGE,"E75")])],"isStart":false});
            var Q12;
            Q12=makeQuery(id+"F3.opExtrude","CAP_FACE",FACE,{"disambiguationData":[OSD([sQuery(id+"F1.wireOp",EDGE,"E47.0"),sQuery(id+"F1.wireOp",EDGE,"E47.1"),sQuery(id+"F1.wireOp",EDGE,"E47.2"),sQuery(id+"F1.wireOp",EDGE,"E47.3"),sQuery(id+"F1.wireOp",EDGE,"E47.4"),sQuery(id+"F1.wireOp",EDGE,"E47.5"),sQuery(id+"F1.wireOp",EDGE,"E47.6"),sQuery(id+"F1.wireOp",EDGE,"E47.7"),sQuery(id+"F1.wireOp",EDGE,"E67"),sQuery(id+"F1.wireOp",EDGE,"E68")])],"isStart":false});
            var Q13;
            Q13=makeQuery(id+"F3.opExtrude","CAP_FACE",FACE,{"disambiguationData":[OSD([sQuery(id+"F1.wireOp",EDGE,"E46.13"),sQuery(id+"F1.wireOp",EDGE,"E46.14"),sQuery(id+"F1.wireOp",EDGE,"E46.15"),sQuery(id+"F1.wireOp",EDGE,"E46.16"),sQuery(id+"F1.wireOp",EDGE,"E46.17"),sQuery(id+"F1.wireOp",EDGE,"E46.18"),sQuery(id+"F1.wireOp",EDGE,"E46.19"),sQuery(id+"F1.wireOp",EDGE,"E46.20"),sQuery(id+"F1.wireOp",EDGE,"E63"),sQuery(id+"F1.wireOp",EDGE,"E64"),sQuery(id+"F1.wireOp",EDGE,"E65"),sQuery(id+"F1.wireOp",EDGE,"E66")])],"isStart":false});
            var Q14;
            Q14=makeQuery(id+"F3.opExtrude","CAP_FACE",FACE,{"disambiguationData":[OSD([sQuery(id+"F1.wireOp",EDGE,"E43.0"),sQuery(id+"F1.wireOp",EDGE,"E43.1"),sQuery(id+"F1.wireOp",EDGE,"E43.2"),sQuery(id+"F1.wireOp",EDGE,"E43.4"),sQuery(id+"F1.wireOp",EDGE,"E44"),sQuery(id+"F1.wireOp",EDGE,"E45"),sQuery(id+"F1.wireOp",EDGE,"E57"),sQuery(id+"F1.wireOp",EDGE,"E58"),sQuery(id+"F1.wireOp",EDGE,"E59"),sQuery(id+"F1.wireOp",EDGE,"E60"),sQuery(id+"F1.wireOp",EDGE,"E61"),sQuery(id+"F1.wireOp",EDGE,"E62"),sQuery(id+"F1.wireOp",EDGE,"E76"),sQuery(id+"F1.wireOp",EDGE,"E77"),sQuery(id+"F1.wireOp",EDGE,"E78"),sQuery(id+"F1.wireOp",EDGE,"E79")])],"isStart":false});
            var Q15;
            Q15=makeQuery(id+"F5.opExtrude","CAP_FACE",FACE,{"disambiguationData":[OSD([sQuery(id+"F4.wireOp",EDGE,"E129.bottom"),sQuery(id+"F4.wireOp",EDGE,"E129.top"),sQuery(id+"F4.wireOp",EDGE,"E129.left"),sQuery(id+"F4.wireOp",EDGE,"E129.right"),sQuery(id+"F4.wireOp",EDGE,"E130.filletArc"),sQuery(id+"F4.wireOp",EDGE,"E131.filletArc"),sQuery(id+"F4.wireOp",EDGE,"E132.filletArc"),sQuery(id+"F4.wireOp",EDGE,"E133.filletArc")])],"isStart":true});
            chamfer(context, id + "F6", {"entities" : qUnion([Q0, Q1, Q2, Q3, Q4, Q5, Q6, Q7, Q8, Q9, Q10, Q11, Q12, Q13, Q14, Q15]), "width" : 0.4 * mm, "tangentPropagation" : true});
        }
        {
            var Q0;
            Q0=makeQuery(id+"F3.opExtrude","SWEPT_BODY",BODY,{"disambiguationData":[OSD([sQuery(id+"F0.wireOp",EDGE,"E0.0"),sQuery(id+"F0.wireOp",EDGE,"E0.1"),sQuery(id+"F0.wireOp",EDGE,"E0.2"),sQuery(id+"F0.wireOp",EDGE,"E0.4"),sQuery(id+"F0.wireOp",EDGE,"E1"),sQuery(id+"F0.wireOp",EDGE,"E2"),sQuery(id+"F0.wireOp",EDGE,"E14"),sQuery(id+"F0.wireOp",EDGE,"E15"),sQuery(id+"F0.wireOp",EDGE,"E16"),sQuery(id+"F0.wireOp",EDGE,"E17"),sQuery(id+"F0.wireOp",EDGE,"E18"),sQuery(id+"F0.wireOp",EDGE,"E19"),sQuery(id+"F0.wireOp",EDGE,"E33"),sQuery(id+"F0.wireOp",EDGE,"E34"),sQuery(id+"F0.wireOp",EDGE,"E35"),sQuery(id+"F0.wireOp",EDGE,"E36")])]});
            var Q1;
            Q1=makeQuery(id+"F3.opExtrude","SWEPT_BODY",BODY,{"disambiguationData":[OSD([sQuery(id+"F0.wireOp",EDGE,"E3.13"),sQuery(id+"F0.wireOp",EDGE,"E3.14"),sQuery(id+"F0.wireOp",EDGE,"E3.15"),sQuery(id+"F0.wireOp",EDGE,"E3.16"),sQuery(id+"F0.wireOp",EDGE,"E3.17"),sQuery(id+"F0.wireOp",EDGE,"E3.18"),sQuery(id+"F0.wireOp",EDGE,"E3.19"),sQuery(id+"F0.wireOp",EDGE,"E3.20"),sQuery(id+"F0.wireOp",EDGE,"E20"),sQuery(id+"F0.wireOp",EDGE,"E21"),sQuery(id+"F0.wireOp",EDGE,"E22"),sQuery(id+"F0.wireOp",EDGE,"E23")])]});
            var Q2;
            Q2=makeQuery(id+"F3.opExtrude","SWEPT_BODY",BODY,{"disambiguationData":[OSD([sQuery(id+"F0.wireOp",EDGE,"E4.0"),sQuery(id+"F0.wireOp",EDGE,"E4.1"),sQuery(id+"F0.wireOp",EDGE,"E4.2"),sQuery(id+"F0.wireOp",EDGE,"E4.3"),sQuery(id+"F0.wireOp",EDGE,"E4.4"),sQuery(id+"F0.wireOp",EDGE,"E4.5"),sQuery(id+"F0.wireOp",EDGE,"E4.6"),sQuery(id+"F0.wireOp",EDGE,"E4.7"),sQuery(id+"F0.wireOp",EDGE,"E24"),sQuery(id+"F0.wireOp",EDGE,"E25")])]});
            var Q3;
            Q3=makeQuery(id+"F3.opExtrude","SWEPT_BODY",BODY,{"disambiguationData":[OSD([sQuery(id+"F0.wireOp",EDGE,"E5.0"),sQuery(id+"F0.wireOp",EDGE,"E5.1"),sQuery(id+"F0.wireOp",EDGE,"E5.2"),sQuery(id+"F0.wireOp",EDGE,"E5.3"),sQuery(id+"F0.wireOp",EDGE,"E5.4"),sQuery(id+"F0.wireOp",EDGE,"E5.5"),sQuery(id+"F0.wireOp",EDGE,"E5.6"),sQuery(id+"F0.wireOp",EDGE,"E5.7"),sQuery(id+"F0.wireOp",EDGE,"E5.8"),sQuery(id+"F0.wireOp",EDGE,"E5.9"),sQuery(id+"F0.wireOp",EDGE,"E5.10"),sQuery(id+"F0.wireOp",EDGE,"E26"),sQuery(id+"F0.wireOp",EDGE,"E32")])]});
            var Q4;
            Q4=makeQuery(id+"F3.opExtrude","SWEPT_BODY",BODY,{"disambiguationData":[OSD([sQuery(id+"F0.wireOp",EDGE,"E6.0"),sQuery(id+"F0.wireOp",EDGE,"E6.1"),sQuery(id+"F0.wireOp",EDGE,"E6.2"),sQuery(id+"F0.wireOp",EDGE,"E6.3"),sQuery(id+"F0.wireOp",EDGE,"E6.4"),sQuery(id+"F0.wireOp",EDGE,"E6.5"),sQuery(id+"F0.wireOp",EDGE,"E6.6"),sQuery(id+"F0.wireOp",EDGE,"E6.7"),sQuery(id+"F0.wireOp",EDGE,"E6.8"),sQuery(id+"F0.wireOp",EDGE,"E6.9"),sQuery(id+"F0.wireOp",EDGE,"E6.10"),sQuery(id+"F0.wireOp",EDGE,"E6.11"),sQuery(id+"F0.wireOp",EDGE,"E27"),sQuery(id+"F0.wireOp",EDGE,"E28"),sQuery(id+"F0.wireOp",EDGE,"E29"),sQuery(id+"F0.wireOp",EDGE,"E30")])]});
            var Q5;
            Q5=makeQuery(id+"F3.opExtrude","SWEPT_BODY",BODY,{"disambiguationData":[OSD([sQuery(id+"F1.wireOp",EDGE,"E43.0"),sQuery(id+"F1.wireOp",EDGE,"E43.1"),sQuery(id+"F1.wireOp",EDGE,"E43.2"),sQuery(id+"F1.wireOp",EDGE,"E43.4"),sQuery(id+"F1.wireOp",EDGE,"E44"),sQuery(id+"F1.wireOp",EDGE,"E45"),sQuery(id+"F1.wireOp",EDGE,"E57"),sQuery(id+"F1.wireOp",EDGE,"E58"),sQuery(id+"F1.wireOp",EDGE,"E59"),sQuery(id+"F1.wireOp",EDGE,"E60"),sQuery(id+"F1.wireOp",EDGE,"E61"),sQuery(id+"F1.wireOp",EDGE,"E62"),sQuery(id+"F1.wireOp",EDGE,"E76"),sQuery(id+"F1.wireOp",EDGE,"E77"),sQuery(id+"F1.wireOp",EDGE,"E78"),sQuery(id+"F1.wireOp",EDGE,"E79")])]});
            var Q6;
            Q6=makeQuery(id+"F3.opExtrude","SWEPT_BODY",BODY,{"disambiguationData":[OSD([sQuery(id+"F1.wireOp",EDGE,"E49.0"),sQuery(id+"F1.wireOp",EDGE,"E49.1"),sQuery(id+"F1.wireOp",EDGE,"E49.2"),sQuery(id+"F1.wireOp",EDGE,"E49.3"),sQuery(id+"F1.wireOp",EDGE,"E49.4"),sQuery(id+"F1.wireOp",EDGE,"E49.5"),sQuery(id+"F1.wireOp",EDGE,"E49.6"),sQuery(id+"F1.wireOp",EDGE,"E49.7"),sQuery(id+"F1.wireOp",EDGE,"E49.8"),sQuery(id+"F1.wireOp",EDGE,"E49.9"),sQuery(id+"F1.wireOp",EDGE,"E49.10"),sQuery(id+"F1.wireOp",EDGE,"E49.11"),sQuery(id+"F1.wireOp",EDGE,"E70"),sQuery(id+"F1.wireOp",EDGE,"E71"),sQuery(id+"F1.wireOp",EDGE,"E72"),sQuery(id+"F1.wireOp",EDGE,"E73")])]});
            var Q7;
            Q7=makeQuery(id+"F3.opExtrude","SWEPT_BODY",BODY,{"disambiguationData":[OSD([sQuery(id+"F1.wireOp",EDGE,"E48.0"),sQuery(id+"F1.wireOp",EDGE,"E48.1"),sQuery(id+"F1.wireOp",EDGE,"E48.2"),sQuery(id+"F1.wireOp",EDGE,"E48.3"),sQuery(id+"F1.wireOp",EDGE,"E48.4"),sQuery(id+"F1.wireOp",EDGE,"E48.5"),sQuery(id+"F1.wireOp",EDGE,"E48.6"),sQuery(id+"F1.wireOp",EDGE,"E48.7"),sQuery(id+"F1.wireOp",EDGE,"E48.8"),sQuery(id+"F1.wireOp",EDGE,"E48.9"),sQuery(id+"F1.wireOp",EDGE,"E48.10"),sQuery(id+"F1.wireOp",EDGE,"E69"),sQuery(id+"F1.wireOp",EDGE,"E75")])]});
            var Q8;
            Q8=makeQuery(id+"F3.opExtrude","SWEPT_BODY",BODY,{"disambiguationData":[OSD([sQuery(id+"F1.wireOp",EDGE,"E47.0"),sQuery(id+"F1.wireOp",EDGE,"E47.1"),sQuery(id+"F1.wireOp",EDGE,"E47.2"),sQuery(id+"F1.wireOp",EDGE,"E47.3"),sQuery(id+"F1.wireOp",EDGE,"E47.4"),sQuery(id+"F1.wireOp",EDGE,"E47.5"),sQuery(id+"F1.wireOp",EDGE,"E47.6"),sQuery(id+"F1.wireOp",EDGE,"E47.7"),sQuery(id+"F1.wireOp",EDGE,"E67"),sQuery(id+"F1.wireOp",EDGE,"E68")])]});
            var Q9;
            Q9=makeQuery(id+"F3.opExtrude","SWEPT_BODY",BODY,{"disambiguationData":[OSD([sQuery(id+"F1.wireOp",EDGE,"E46.13"),sQuery(id+"F1.wireOp",EDGE,"E46.14"),sQuery(id+"F1.wireOp",EDGE,"E46.15"),sQuery(id+"F1.wireOp",EDGE,"E46.16"),sQuery(id+"F1.wireOp",EDGE,"E46.17"),sQuery(id+"F1.wireOp",EDGE,"E46.18"),sQuery(id+"F1.wireOp",EDGE,"E46.19"),sQuery(id+"F1.wireOp",EDGE,"E46.20"),sQuery(id+"F1.wireOp",EDGE,"E63"),sQuery(id+"F1.wireOp",EDGE,"E64"),sQuery(id+"F1.wireOp",EDGE,"E65"),sQuery(id+"F1.wireOp",EDGE,"E66")])]});
            var Q10;
            Q10=makeQuery(id+"F3.opExtrude","SWEPT_BODY",BODY,{"disambiguationData":[OSD([sQuery(id+"F2.wireOp",EDGE,"E92.0"),sQuery(id+"F2.wireOp",EDGE,"E92.1"),sQuery(id+"F2.wireOp",EDGE,"E92.2"),sQuery(id+"F2.wireOp",EDGE,"E92.3"),sQuery(id+"F2.wireOp",EDGE,"E92.4"),sQuery(id+"F2.wireOp",EDGE,"E92.5"),sQuery(id+"F2.wireOp",EDGE,"E92.6"),sQuery(id+"F2.wireOp",EDGE,"E92.7"),sQuery(id+"F2.wireOp",EDGE,"E92.8"),sQuery(id+"F2.wireOp",EDGE,"E92.9"),sQuery(id+"F2.wireOp",EDGE,"E92.10"),sQuery(id+"F2.wireOp",EDGE,"E92.11"),sQuery(id+"F2.wireOp",EDGE,"E113"),sQuery(id+"F2.wireOp",EDGE,"E114"),sQuery(id+"F2.wireOp",EDGE,"E115"),sQuery(id+"F2.wireOp",EDGE,"E116")])]});
            var Q11;
            Q11=makeQuery(id+"F3.opExtrude","SWEPT_BODY",BODY,{"disambiguationData":[OSD([sQuery(id+"F2.wireOp",EDGE,"E91.0"),sQuery(id+"F2.wireOp",EDGE,"E91.1"),sQuery(id+"F2.wireOp",EDGE,"E91.2"),sQuery(id+"F2.wireOp",EDGE,"E91.3"),sQuery(id+"F2.wireOp",EDGE,"E91.4"),sQuery(id+"F2.wireOp",EDGE,"E91.5"),sQuery(id+"F2.wireOp",EDGE,"E91.6"),sQuery(id+"F2.wireOp",EDGE,"E91.7"),sQuery(id+"F2.wireOp",EDGE,"E91.8"),sQuery(id+"F2.wireOp",EDGE,"E91.9"),sQuery(id+"F2.wireOp",EDGE,"E91.10"),sQuery(id+"F2.wireOp",EDGE,"E112"),sQuery(id+"F2.wireOp",EDGE,"E118")])]});
            var Q12;
            Q12=makeQuery(id+"F3.opExtrude","SWEPT_BODY",BODY,{"disambiguationData":[OSD([sQuery(id+"F2.wireOp",EDGE,"E90.0"),sQuery(id+"F2.wireOp",EDGE,"E90.1"),sQuery(id+"F2.wireOp",EDGE,"E90.2"),sQuery(id+"F2.wireOp",EDGE,"E90.3"),sQuery(id+"F2.wireOp",EDGE,"E90.4"),sQuery(id+"F2.wireOp",EDGE,"E90.5"),sQuery(id+"F2.wireOp",EDGE,"E90.6"),sQuery(id+"F2.wireOp",EDGE,"E90.7"),sQuery(id+"F2.wireOp",EDGE,"E110"),sQuery(id+"F2.wireOp",EDGE,"E111")])]});
            var Q13;
            Q13=makeQuery(id+"F3.opExtrude","SWEPT_BODY",BODY,{"disambiguationData":[OSD([sQuery(id+"F2.wireOp",EDGE,"E89.13"),sQuery(id+"F2.wireOp",EDGE,"E89.14"),sQuery(id+"F2.wireOp",EDGE,"E89.15"),sQuery(id+"F2.wireOp",EDGE,"E89.16"),sQuery(id+"F2.wireOp",EDGE,"E89.17"),sQuery(id+"F2.wireOp",EDGE,"E89.18"),sQuery(id+"F2.wireOp",EDGE,"E89.19"),sQuery(id+"F2.wireOp",EDGE,"E89.20"),sQuery(id+"F2.wireOp",EDGE,"E106"),sQuery(id+"F2.wireOp",EDGE,"E107"),sQuery(id+"F2.wireOp",EDGE,"E108"),sQuery(id+"F2.wireOp",EDGE,"E109")])]});
            var Q14;
            Q14=makeQuery(id+"F3.opExtrude","SWEPT_BODY",BODY,{"disambiguationData":[OSD([sQuery(id+"F2.wireOp",EDGE,"E86.0"),sQuery(id+"F2.wireOp",EDGE,"E86.1"),sQuery(id+"F2.wireOp",EDGE,"E86.2"),sQuery(id+"F2.wireOp",EDGE,"E86.4"),sQuery(id+"F2.wireOp",EDGE,"E87"),sQuery(id+"F2.wireOp",EDGE,"E88"),sQuery(id+"F2.wireOp",EDGE,"E100"),sQuery(id+"F2.wireOp",EDGE,"E101"),sQuery(id+"F2.wireOp",EDGE,"E102"),sQuery(id+"F2.wireOp",EDGE,"E103"),sQuery(id+"F2.wireOp",EDGE,"E104"),sQuery(id+"F2.wireOp",EDGE,"E105"),sQuery(id+"F2.wireOp",EDGE,"E119"),sQuery(id+"F2.wireOp",EDGE,"E120"),sQuery(id+"F2.wireOp",EDGE,"E121"),sQuery(id+"F2.wireOp",EDGE,"E122")])]});
            var Q15;
            Q15=makeQuery(id+"F5.opExtrude","SWEPT_BODY",BODY,{"disambiguationData":[OSD([sQuery(id+"F4.wireOp",EDGE,"E129.bottom"),sQuery(id+"F4.wireOp",EDGE,"E129.top"),sQuery(id+"F4.wireOp",EDGE,"E129.left"),sQuery(id+"F4.wireOp",EDGE,"E129.right")])]});
            booleanBodies(context, id + "F7", {"operationType" : BooleanOperationType.SUBTRACTION, "tools" : qUnion([Q0, Q1, Q2, Q3, Q4, Q5, Q6, Q7, Q8, Q9, Q10, Q11, Q12, Q13, Q14]), "targets" : qUnion([Q15]), "offset" : true, "offsetAll" : true, "offsetDistance" : .1 * mm});
        }
    });
